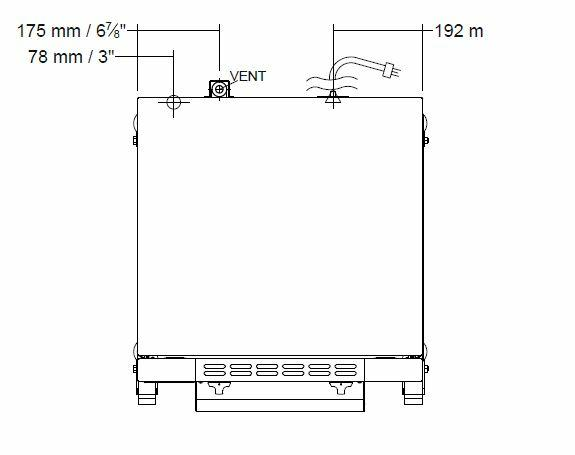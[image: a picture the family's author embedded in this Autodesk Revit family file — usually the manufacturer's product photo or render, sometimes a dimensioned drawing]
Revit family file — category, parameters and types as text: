
# Revit family: QF_MOFFAT_E28D4-2C_NZ
name_source: partatom
category: Specialty Equipment
revit_build: Autodesk Revit 2014 (Build: 20130308_1515(x64)
units: mm (PartAtom-declared; Revit-internal decimal feet)

## types (1)
- QF_MOFFAT_E28D4-2C_NZ
    Apparent Power = 5750 VA
    Cold Water Connection Height = 0 mm  [stored 0 ft]
    Cold Water Flow = 0 GPM
    Cold Water Maximum Pressure = 80.00 psi
    Cold Water Minimum Pressure = 20.00 psi
    Cold Water RI Height = 0 mm  [stored 0 ft]
    Cold Water Size = 1"
    Cold Water Temperature Recommended = 0 °F
    Conn Conduit = Yes
    Cycle = 50 Hz
    Depth = 762 mm  [stored 2.5 ft]
    Description = FULL SIZE DIGITAL / ELECTRIC CONVECTION OVENS DOUBLE STACKED ON A STAINLESS STEEL BASE STAND
    Elec Conn Connection Height = 0 mm  [stored 0 ft]
    Elec Conn RI Height = 0 mm  [stored 0 ft]
    Electrical Remarks = 230-240V, 50Hz, 1P+N+E, 5.8kW, 25A
    Exhaust RI Height = 0 mm  [stored 0 ft]
    Exhaust Static Press = 0.00 in-wg
    Exhaust Vent Depth = 0 mm  [stored 0 ft]
    Exhaust Vent Diameter = 0 mm  [stored 0 ft]
    Exhaust Vent Width = 0 mm  [stored 0 ft]
    Exhaust Volume = 0 CFM
    FL Amps = 25 A
    Foodservice Equipment Identifier = Yes
    Height = 1763 mm
    Height of Stand = 536 mm  [stored 1.75853 ft]
    Identify Quantity as Lot = Yes
    Length = 810 mm  [stored 2.65748 ft]
    Manufacturer = MOFFAT
    Max Overcurrent Protection = 0 A
    Min Ckt Ampacity = 0 A
    Model = E28D4-2C
    Number of Poles = 1
    Phase = 1
    URL = www.moffat.com.au
    URL Cutsheet = www.moffat.com.au
    Volts = 230 V
    Watts = 5800 W
    Weight in Pounds = 0

note: [stored X ft] marks values corroborated as IEEE doubles in the binary element streams (Revit-internal decimal feet)

## geometry (parser evidence)
native form markers: Blend x16, Sweep x7
no freeform markers — native parametric forms only
